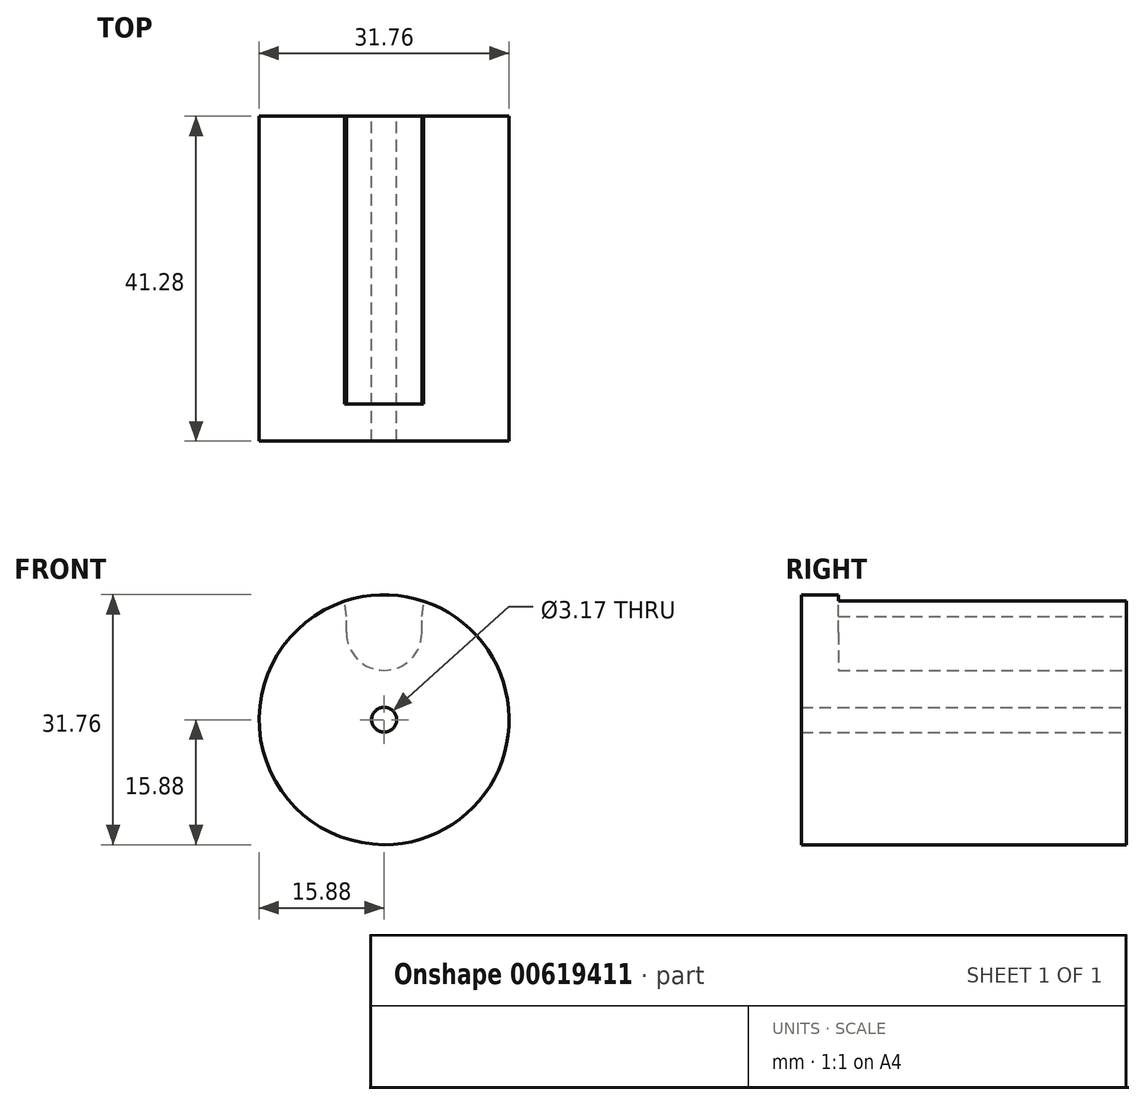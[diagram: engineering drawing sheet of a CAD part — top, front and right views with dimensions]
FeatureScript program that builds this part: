
annotation { "Feature Type Name" : "Feature", "Feature Type Description" : "" }
export const myFeature = defineFeature(function(context is Context, id is Id, definition is map)
    precondition{}
    {
        {
            var Q0;
            Q0=qCreatedBy(makeId("Front.planeOp"),FACE);
            var sketch = newSketch(context, id + "F0", { "sketchPlane" : qUnion([Q0])});
            skCircle(sketch, "E0", {"center": v(0, 0) * mm, "radius": 15.88 * mm});
            skLineSegment(sketch, "E1", {"start": v(0, 15.88) * mm, "end": v(0, 11.07) * mm});
            skCircle(sketch, "E2", {"center": v(0, 11.07) * mm, "radius": 4.8 * mm});
            skLineSegment(sketch, "E3", {"start": v(-4.8, 11.07) * mm, "end": v(-4.8, 15.13) * mm});
            skLineSegment(sketch, "E4.MirrorCS", {"start": v(4.8, 11.07) * mm, "end": v(4.8, 15.13) * mm});
            skLineSegment(sketch, "E5", {"start": v(-4.8, 13.1) * mm, "end": v(-5.03, 15.06) * mm});
            skLineSegment(sketch, "E6.MirrorCS", {"start": v(4.8, 13.1) * mm, "end": v(5.03, 15.06) * mm});
            skCircle(sketch, "E7", {"center": v(0, 0) * mm, "radius": 1.59 * mm});
            skSolve(sketch);
        }
        {
            var Q0;
            {var subQ6=sQuery(id+"F0.wireOp",EDGE,"E5");Q0=makeQuery(id+"F0.imprint","IMPRINT",FACE,{"disambiguationData":[TD([[makeQuery(id+"F0.imprint","IMPRINT",EDGE,{"derivedFrom":subQ6}),1.0]])]});}
            var Q1;
            {var subQ0=sQuery(id+"F0.wireOp",EDGE,"E2");var subQ1=sQuery(id+"F0.wireOp",EDGE,"E0");var subQ2=makeQuery(id+"F0.imprint","INTERSECT",VERTEX,{"derivedFrom":[subQ1,subQ0]});Q1=makeQuery(id+"F0.imprint","IMPRINT",FACE,{"disambiguationData":[TD([[makeQuery(id+"F0.imprint","IMPRINT",EDGE,{"disambiguationData":[TD([[subQ2,-1.0]])],"derivedFrom":subQ1}),1.0]])]});}
            var Q2;
            {var subQ3=sQuery(id+"F0.wireOp",EDGE,"E5");Q2=makeQuery(id+"F0.imprint","IMPRINT",FACE,{"disambiguationData":[TD([[makeQuery(id+"F0.imprint","IMPRINT",EDGE,{"derivedFrom":subQ3}),-1.0]])]});}
            var Q3;
            {var subQ0=sQuery(id+"F0.wireOp",EDGE,"E2");var subQ1=makeQuery(id+"F0.imprint","INTERSECT",VERTEX,{"derivedFrom":[sQuery(id+"F0.wireOp",EDGE,"E0"),subQ0]});Q3=makeQuery(id+"F0.imprint","IMPRINT",FACE,{"disambiguationData":[TD([[makeQuery(id+"F0.imprint","IMPRINT",EDGE,{"disambiguationData":[TD([[subQ1,1.0]])],"derivedFrom":subQ0}),1.0]])]});}
            var Q4;
            {var subQ3=sQuery(id+"F0.wireOp",EDGE,"E6.MirrorCS");Q4=makeQuery(id+"F0.imprint","IMPRINT",FACE,{"disambiguationData":[TD([[makeQuery(id+"F0.imprint","IMPRINT",EDGE,{"derivedFrom":subQ3}),1.0]])]});}
            var Q5;
            {var subQ0=sQuery(id+"F0.wireOp",EDGE,"E2");var subQ1=sQuery(id+"F0.wireOp",EDGE,"E0");var subQ2=makeQuery(id+"F0.imprint","INTERSECT",VERTEX,{"derivedFrom":[subQ1,subQ0]});Q5=makeQuery(id+"F0.imprint","IMPRINT",FACE,{"disambiguationData":[TD([[makeQuery(id+"F0.imprint","IMPRINT",EDGE,{"disambiguationData":[TD([[subQ2,1.0]])],"derivedFrom":subQ1}),1.0]])]});}
            extrude(context, id + "F1", {"entities" : qUnion([Q0, Q1, Q2, Q3, Q4, Q5]), "depth" : 41.27 * mm, "offsetDistance" : 25.4 * mm});
        }
        {
            var Q0;
            {var subQ0=sQuery(id+"F0.wireOp",EDGE,"E2");var subQ1=makeQuery(id+"F0.imprint","INTERSECT",VERTEX,{"derivedFrom":[sQuery(id+"F0.wireOp",EDGE,"E0"),subQ0]});Q0=makeQuery(id+"F0.imprint","IMPRINT",FACE,{"disambiguationData":[TD([[makeQuery(id+"F0.imprint","IMPRINT",EDGE,{"disambiguationData":[TD([[subQ1,1.0]])],"derivedFrom":subQ0}),1.0]])]});}
            var Q1;
            {var subQ0=sQuery(id+"F0.wireOp",EDGE,"E2");var subQ1=sQuery(id+"F0.wireOp",EDGE,"E0");var subQ2=makeQuery(id+"F0.imprint","INTERSECT",VERTEX,{"derivedFrom":[subQ1,subQ0]});Q1=makeQuery(id+"F0.imprint","IMPRINT",FACE,{"disambiguationData":[TD([[makeQuery(id+"F0.imprint","IMPRINT",EDGE,{"disambiguationData":[TD([[subQ2,-1.0]])],"derivedFrom":subQ1}),1.0]])]});}
            var Q2;
            {var subQ0=sQuery(id+"F0.wireOp",EDGE,"E2");var subQ1=sQuery(id+"F0.wireOp",EDGE,"E0");var subQ2=makeQuery(id+"F0.imprint","INTERSECT",VERTEX,{"derivedFrom":[subQ1,subQ0]});Q2=makeQuery(id+"F0.imprint","IMPRINT",FACE,{"disambiguationData":[TD([[makeQuery(id+"F0.imprint","IMPRINT",EDGE,{"disambiguationData":[TD([[subQ2,1.0]])],"derivedFrom":subQ1}),1.0]])]});}
            var Q3;
            {var subQ3=sQuery(id+"F0.wireOp",EDGE,"E5");Q3=makeQuery(id+"F0.imprint","IMPRINT",FACE,{"disambiguationData":[TD([[makeQuery(id+"F0.imprint","IMPRINT",EDGE,{"derivedFrom":subQ3}),-1.0]])]});}
            var Q4;
            {var subQ3=sQuery(id+"F0.wireOp",EDGE,"E6.MirrorCS");Q4=makeQuery(id+"F0.imprint","IMPRINT",FACE,{"disambiguationData":[TD([[makeQuery(id+"F0.imprint","IMPRINT",EDGE,{"derivedFrom":subQ3}),1.0]])]});}
            extrude(context, id + "F2", {"entities" : qUnion([Q0, Q1, Q2, Q3, Q4]), "operationType" : NewBodyOperationType.REMOVE, "depth" : 36.58 * mm, "offsetDistance" : 25.4 * mm});
        }
    });
